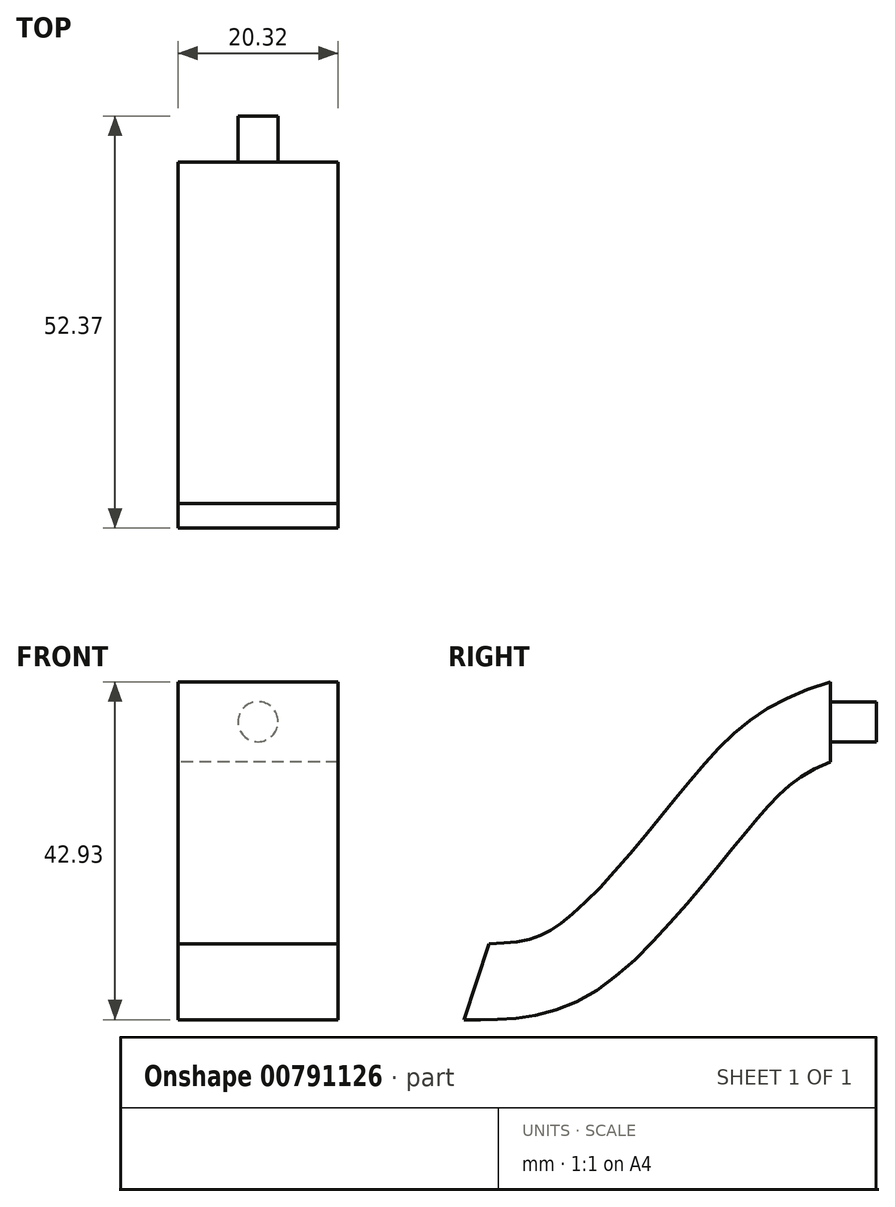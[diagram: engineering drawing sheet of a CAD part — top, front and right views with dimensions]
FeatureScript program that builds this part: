
annotation { "Feature Type Name" : "Feature", "Feature Type Description" : "" }
export const myFeature = defineFeature(function(context is Context, id is Id, definition is map)
    precondition{}
    {
        {
            var Q0;
            Q0=qCreatedBy(makeId("Right.planeOp"),FACE);
            var sketch = newSketch(context, id + "F0", { "sketchPlane" : qUnion([Q0])});
            skFitSpline(sketch, "E0", {"points": [v(0, 0) * mm, v(-14.13, -10.62) * mm, v(-32.56, -30.2) * mm, v(-44.95, -33.02) * mm], "startDerivative": vector(-60.1, -20.38) * mm, "endDerivative": vector(-46.47, -0.5) * mm});
            skSolve(sketch);
        }
        {
            var Q0;
            Q0=qCreatedBy(makeId("Front.planeOp"),FACE);
            var sketch = newSketch(context, id + "F1", { "sketchPlane" : qUnion([Q0])});
            skLineSegment(sketch, "E1.bottom", {"start": v(10.16, -5.08) * mm, "end": v(-10.16, -5.08) * mm});
            skLineSegment(sketch, "E1.top", {"start": v(10.16, 5.08) * mm, "end": v(-10.16, 5.08) * mm});
            skLineSegment(sketch, "E1.left", {"start": v(10.16, -5.08) * mm, "end": v(10.16, 5.08) * mm});
            skLineSegment(sketch, "E1.right", {"start": v(-10.16, -5.08) * mm, "end": v(-10.16, 5.08) * mm});
            skPoint(sketch, "E1.middle", {"position": v(0, 0) * mm});
            skSolve(sketch);
        }
        {
            var Q0;
            Q0 = qSketchRegion(id + "F1", true);
            var Q1;
            Q1 = qConstructionFilter(qBodyType(qCreatedBy(id + "F0" ,EDGE), BodyType.WIRE), ConstructionObject.NO);
            sweep(context, id + "F2", {"profiles" : qUnion([Q0]), "path" : qUnion([Q1])});
        }
        {
            var Q0;
            Q0=makeQuery(id+"F2.opSweep","CAP_FACE",FACE,{"disambiguationData":[OSD([sQuery(id+"F0.wireOp",VERTEX,"E0.start"),sQuery(id+"F1.wireOp",EDGE,"E1.bottom"),sQuery(id+"F1.wireOp",EDGE,"E1.top"),sQuery(id+"F1.wireOp",EDGE,"E1.left"),sQuery(id+"F1.wireOp",EDGE,"E1.right")])],"isStart":true});
            var sketch = newSketch(context, id + "F3", { "sketchPlane" : qUnion([Q0])});
            skCircle(sketch, "E2", {"center": v(0, 0) * mm, "radius": 2.54 * mm});
            skSolve(sketch);
        }
        {
            var Q0;
            Q0 = qSketchRegion(id + "F3", true);
            extrude(context, id + "F4", {"entities" : qUnion([Q0]), "operationType" : NewBodyOperationType.ADD, "depth" : 5.84 * mm, "offsetDistance" : 25.4 * mm});
        }
    });
